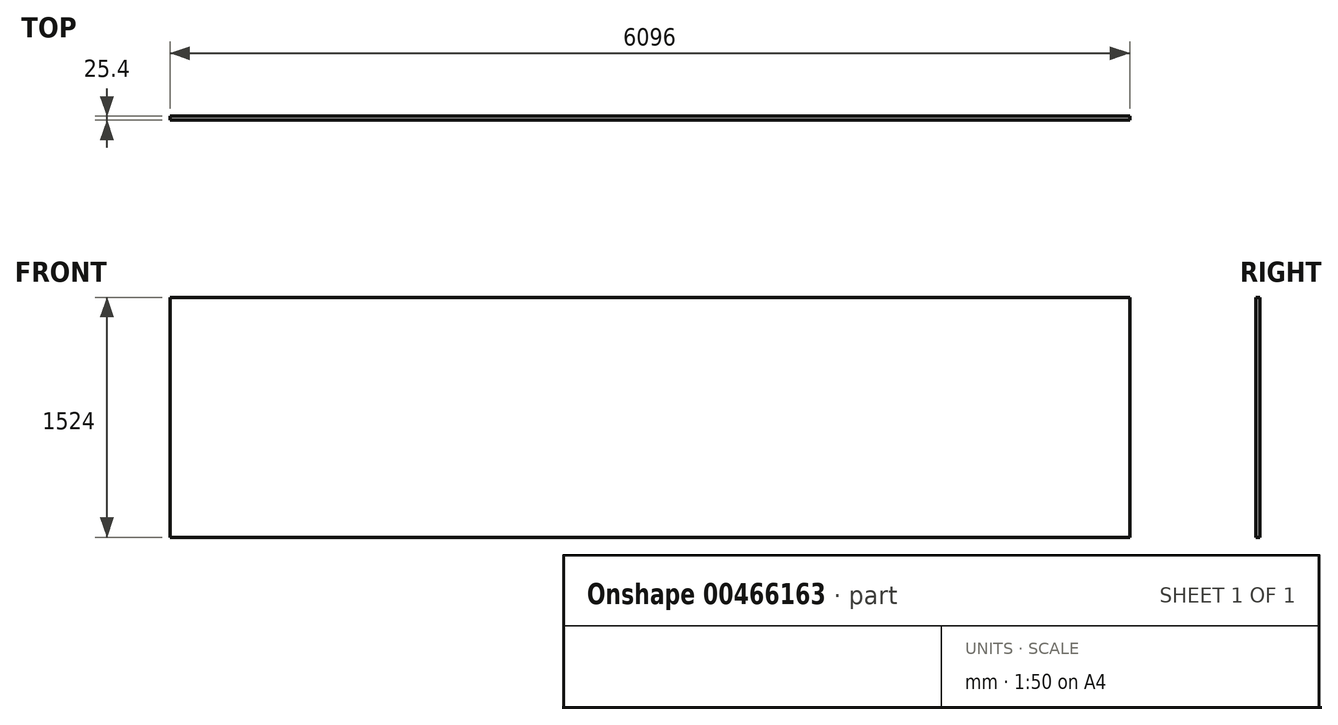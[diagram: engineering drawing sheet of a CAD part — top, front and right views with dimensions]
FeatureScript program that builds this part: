
annotation { "Feature Type Name" : "Feature", "Feature Type Description" : "" }
export const myFeature = defineFeature(function(context is Context, id is Id, definition is map)
    precondition{}
    {
        {
            var Q0;
            Q0=qCreatedBy(makeId("Front.planeOp"),FACE);
            var sketch = newSketch(context, id + "F0", { "sketchPlane" : qUnion([Q0])});
            skLineSegment(sketch, "E0.bottom", {"start": v(0, 0) * mm, "end": v(6096, 0) * mm});
            skLineSegment(sketch, "E0.top", {"start": v(0, 1524) * mm, "end": v(6096, 1524) * mm});
            skLineSegment(sketch, "E0.left", {"start": v(0, 0) * mm, "end": v(0, 1524) * mm});
            skLineSegment(sketch, "E0.right", {"start": v(6096, 0) * mm, "end": v(6096, 1524) * mm});
            skSolve(sketch);
        }
        {
            var Q0;
            Q0=makeQuery(id+"F0.imprint","IMPRINT",FACE,{"disambiguationData":[TD([[makeQuery(id+"F0.imprint","IMPRINT",EDGE,{"derivedFrom":sQuery(id+"F0.wireOp",EDGE,"E0.bottom")}),1.0]])]});
            extrude(context, id + "F1", {"entities" : qUnion([Q0]), "depth" : 25.4 * mm});
        }
    });
